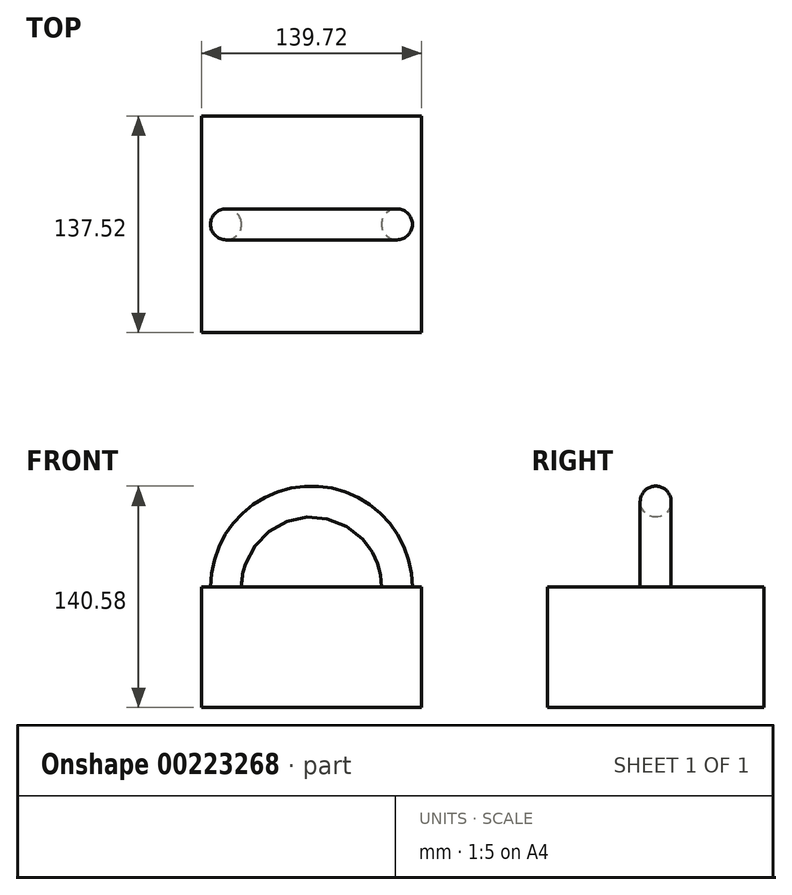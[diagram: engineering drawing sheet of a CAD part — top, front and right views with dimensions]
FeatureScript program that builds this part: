
annotation { "Feature Type Name" : "Feature", "Feature Type Description" : "" }
export const myFeature = defineFeature(function(context is Context, id is Id, definition is map)
    precondition{}
    {
        {
            var Q0;
            Q0=qCreatedBy(makeId("Top.planeOp"),FACE);
            var sketch = newSketch(context, id + "F0", { "sketchPlane" : qUnion([Q0])});
            skLineSegment(sketch, "E0.bottom", {"start": v(69.86, -68.76) * mm, "end": v(-69.86, -68.76) * mm});
            skLineSegment(sketch, "E0.top", {"start": v(69.86, 68.76) * mm, "end": v(-69.86, 68.76) * mm});
            skLineSegment(sketch, "E0.left", {"start": v(69.86, -68.76) * mm, "end": v(69.86, 68.76) * mm});
            skLineSegment(sketch, "E0.right", {"start": v(-69.86, -68.76) * mm, "end": v(-69.86, 68.76) * mm});
            skPoint(sketch, "E0.middle", {"position": v(0, 0) * mm});
            skLineSegment(sketch, "E1", {"start": v(0, 68.76) * mm, "end": v(0, -68.76) * mm});
            skSolve(sketch);
        }
        {
            var Q0;
            Q0=qCreatedBy(makeId("Top.planeOp"),FACE);
            var sketch = newSketch(context, id + "F1", { "sketchPlane" : qUnion([Q0])});
            skCircle(sketch, "E2", {"center": v(54.26, 0) * mm, "radius": 9.82 * mm});
            skSolve(sketch);
        }
        {
            var Q0;
            Q0=makeQuery(id+"F1.imprint","IMPRINT",FACE,{"disambiguationData":[TD([[makeQuery(id+"F1.imprint","IMPRINT",EDGE,{"derivedFrom":sQuery(id+"F1.wireOp",EDGE,"E2")}),1.0]])]});
            var Q1;
            Q1=sQuery(id+"F0.wireOp",EDGE,"E1");
            revolve(context, id + "F2", {"entities" : qUnion([Q0]), "axis" : qUnion([Q1]), "revolveType" : RevolveType.ONE_DIRECTION, "angle" : 180.82 * degree});
        }
        {
            var Q0;
            {var subQ0=sQuery(id+"F0.wireOp",EDGE,"E0.right");Q0=makeQuery(id+"F0.imprint","IMPRINT",FACE,{"disambiguationData":[TD([[makeQuery(id+"F0.imprint","IMPRINT",EDGE,{"derivedFrom":subQ0}),-1.0]])]});}
            var Q1;
            {var subQ0=sQuery(id+"F0.wireOp",EDGE,"E0.left");Q1=makeQuery(id+"F0.imprint","IMPRINT",FACE,{"disambiguationData":[TD([[makeQuery(id+"F0.imprint","IMPRINT",EDGE,{"derivedFrom":subQ0}),1.0]])]});}
            extrude(context, id + "F3", {"entities" : qUnion([Q0, Q1]), "operationType" : NewBodyOperationType.ADD, "oppositeDirection" : true, "depth" : 76.49 * mm});
        }
    });
